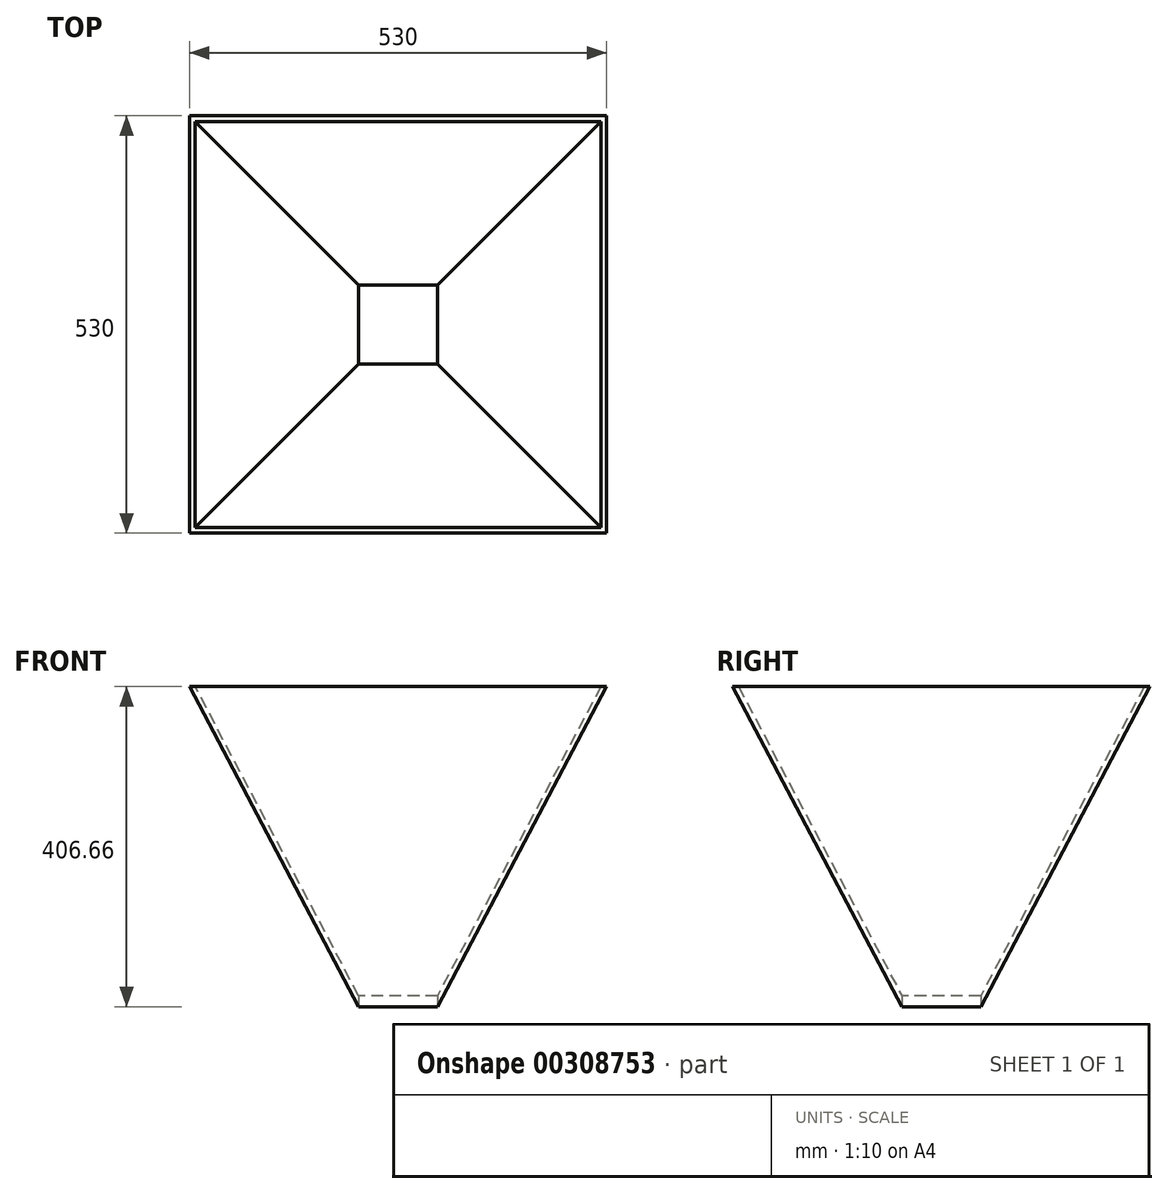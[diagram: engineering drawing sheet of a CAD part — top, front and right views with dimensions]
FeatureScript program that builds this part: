
annotation { "Feature Type Name" : "Feature", "Feature Type Description" : "" }
export const myFeature = defineFeature(function(context is Context, id is Id, definition is map)
    precondition{}
    {
        {
            var Q0;
            Q0=qCreatedBy(makeId("Top.planeOp"),FACE);
            var sketch = newSketch(context, id + "F0", { "sketchPlane" : qUnion([Q0])});
            skLineSegment(sketch, "E0.bottom", {"start": v(50, 50) * mm, "end": v(-50, 50) * mm});
            skLineSegment(sketch, "E0.top", {"start": v(50, -50) * mm, "end": v(-50, -50) * mm});
            skLineSegment(sketch, "E0.left", {"start": v(50, 50) * mm, "end": v(50, -50) * mm});
            skLineSegment(sketch, "E0.right", {"start": v(-50, 50) * mm, "end": v(-50, -50) * mm});
            skPoint(sketch, "E0.middle", {"position": v(0, 0) * mm});
            skSolve(sketch);
        }
        {
            var Q0;
            Q0=qCreatedBy(makeId("Top.planeOp"),FACE);
            cPlane(context, id + "F1", {"entities" : qUnion([Q0]), "cplaneType" : CPlaneType.OFFSET, "offset" : 406.66 * mm, "width" : 152.4 * mm, "height" : 152.4 * mm});
        }
        {
            var Q0;
            Q0=qCreatedBy(id+"F1.planeOp",FACE);
            var sketch = newSketch(context, id + "F2", { "sketchPlane" : qUnion([Q0])});
            skLineSegment(sketch, "E1.bottom", {"start": v(-265, 265) * mm, "end": v(265, 265) * mm});
            skLineSegment(sketch, "E1.top", {"start": v(-265, -265) * mm, "end": v(265, -265) * mm});
            skLineSegment(sketch, "E1.left", {"start": v(-265, 265) * mm, "end": v(-265, -265) * mm});
            skLineSegment(sketch, "E1.right", {"start": v(265, 265) * mm, "end": v(265, -265) * mm});
            skPoint(sketch, "E1.middle", {"position": v(0, 0) * mm});
            skSolve(sketch);
        }
        {
            var Q0;
            Q0=makeQuery(id+"F0.imprint","IMPRINT",FACE,{"disambiguationData":[TD([[makeQuery(id+"F0.imprint","IMPRINT",EDGE,{"derivedFrom":sQuery(id+"F0.wireOp",EDGE,"E0.bottom")}),1.0]])]});
            var Q1;
            Q1=makeQuery(id+"F2.imprint","IMPRINT",FACE,{"disambiguationData":[TD([[makeQuery(id+"F2.imprint","IMPRINT",EDGE,{"derivedFrom":sQuery(id+"F2.wireOp",EDGE,"E1.bottom")}),-1.0]])]});
            loft(context, id + "F3", {"sheetProfilesArray" : [{ "sheetProfileEntities" : qUnion([Q0]) }, { "sheetProfileEntities" : qUnion([Q1]) }]});
        }
        {
            var Q0;
            Q0=makeQuery(id+"F3.opLoft","CAP_FACE",FACE,{"disambiguationData":[OSD([makeQuery(id+"F2.imprint","IMPRINT",FACE,{"disambiguationData":[TD([[makeQuery(id+"F2.imprint","IMPRINT",EDGE,{"derivedFrom":sQuery(id+"F2.wireOp",EDGE,"E1.bottom")}),-1.0]])]})])],"isStart":true});
            shell(context, id + "F4", {"entities" : qUnion([Q0]), "thickness" : 6.35 * mm});
        }
        {
            var Q0;
            Q0=makeQuery(id+"F3.opLoft","CAP_FACE",FACE,{"disambiguationData":[OSD([makeQuery(id+"F0.imprint","IMPRINT",FACE,{"disambiguationData":[TD([[makeQuery(id+"F0.imprint","IMPRINT",EDGE,{"derivedFrom":sQuery(id+"F0.wireOp",EDGE,"E0.bottom")}),1.0]])]})])],"isStart":true});
            extrude(context, id + "F5", {"entities" : qUnion([Q0]), "operationType" : NewBodyOperationType.REMOVE, "oppositeDirection" : true, "depth" : 25.4 * mm});
        }
    });
